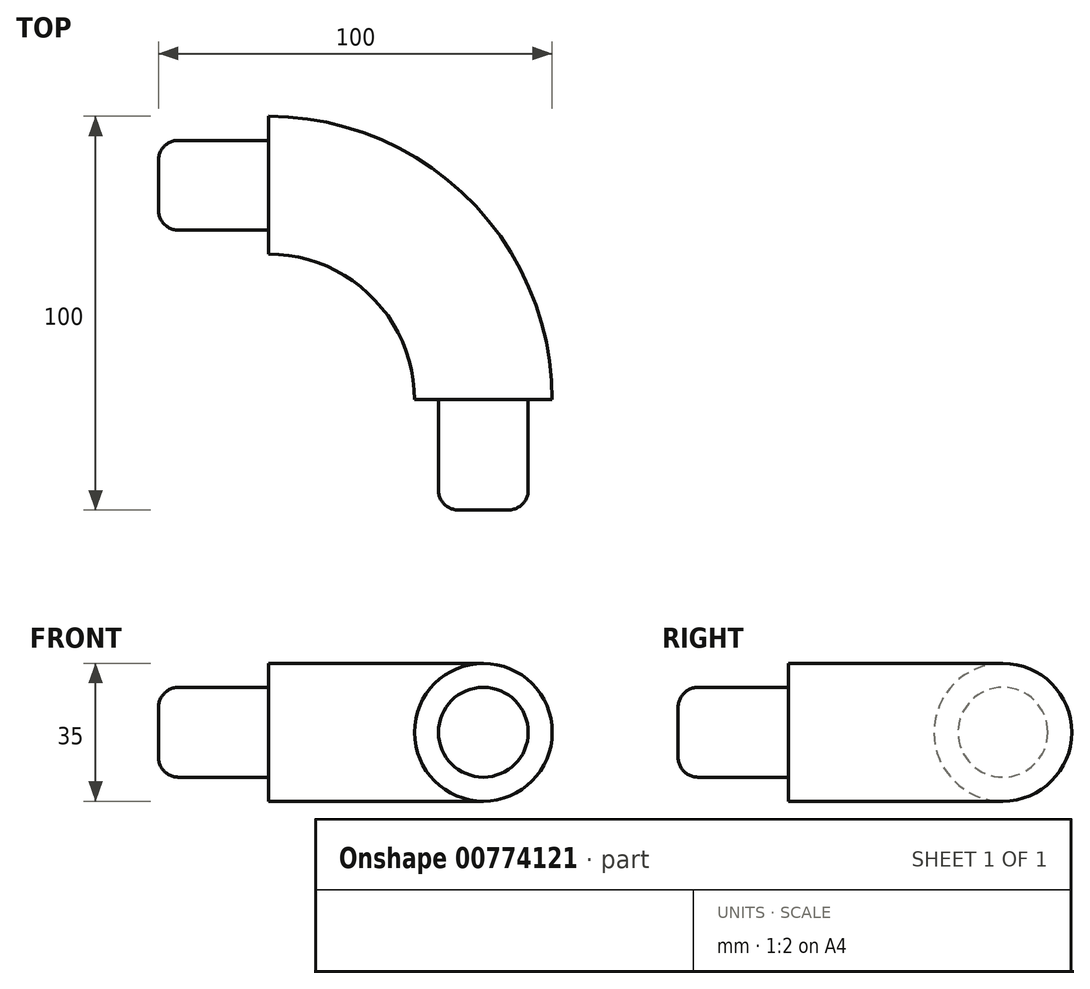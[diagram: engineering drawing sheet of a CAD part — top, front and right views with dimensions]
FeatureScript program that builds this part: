
annotation { "Feature Type Name" : "Feature", "Feature Type Description" : "" }
export const myFeature = defineFeature(function(context is Context, id is Id, definition is map)
    precondition{}
    {
        {
            var Q0;
            Q0=qCreatedBy(makeId("Top.planeOp"),FACE);
            var sketch = newSketch(context, id + "F0", { "sketchPlane" : qUnion([Q0])});
            skArc(sketch, "E0", {"start": v(0, 54.5) * mm, "mid": v(38.54, 38.54) * mm, "end": v(54.5, 0) * mm});
            skSolve(sketch);
        }
        {
            var Q0;
            Q0=qCreatedBy(makeId("Right.planeOp"),FACE);
            var sketch = newSketch(context, id + "F1", { "sketchPlane" : qUnion([Q0])});
            skCircle(sketch, "E1", {"center": v(54.5, 0) * mm, "radius": 17.5 * mm});
            skSolve(sketch);
        }
        {
            var Q0;
            Q0=makeQuery(id+"F1.imprint","IMPRINT",FACE,{"disambiguationData":[TD([[makeQuery(id+"F1.imprint","IMPRINT",EDGE,{"derivedFrom":sQuery(id+"F1.wireOp",EDGE,"E1")}),1.0]])]});
            var Q1;
            Q1=sQuery(id+"F0.wireOp",EDGE,"E0");
            sweep(context, id + "F2", {"profiles" : qUnion([Q0]), "path" : qUnion([Q1])});
        }
        {
            var Q0;
            Q0=makeQuery(id+"F2.opSweep","CAP_FACE",FACE,{"disambiguationData":[OSD([sQuery(id+"F0.wireOp",VERTEX,"E0.end"),sQuery(id+"F1.wireOp",EDGE,"E1")])],"isStart":false});
            var sketch = newSketch(context, id + "F3", { "sketchPlane" : qUnion([Q0])});
            skCircle(sketch, "E2", {"center": v(54.5, 0) * mm, "radius": 11.4 * mm});
            skSolve(sketch);
        }
        {
            var Q0;
            Q0 = qSketchRegion(id + "F3", true);
            extrude(context, id + "F4", {"entities" : qUnion([Q0]), "operationType" : NewBodyOperationType.ADD, "depth" : 28 * mm, "offsetDistance" : 25 * mm});
        }
        {
            var Q0;
            Q0=makeQuery(id+"F2.opSweep","CAP_FACE",FACE,{"disambiguationData":[OSD([sQuery(id+"F0.wireOp",VERTEX,"E0.start"),sQuery(id+"F1.wireOp",EDGE,"E1")])],"isStart":true});
            var sketch = newSketch(context, id + "F5", { "sketchPlane" : qUnion([Q0])});
            skCircle(sketch, "E3", {"center": v(-54.5, 0) * mm, "radius": 11.4 * mm});
            skSolve(sketch);
        }
        {
            var Q0;
            Q0 = qSketchRegion(id + "F5", true);
            extrude(context, id + "F6", {"entities" : qUnion([Q0]), "operationType" : NewBodyOperationType.ADD, "depth" : 28 * mm, "offsetDistance" : 25 * mm});
        }
        {
            var Q0;
            Q0=makeQuery(id+"F4.opExtrude","CAP_EDGE",EDGE,{"disambiguationData":[OSD([sQuery(id+"F3.wireOp",EDGE,"E2")])],"isStart":false});
            fillet(context, id + "F7", {"entities" : qUnion([Q0]), "radius" : 5 * mm, "tangentPropagation" : true, "allowEdgeOverflow" : false});
        }
        {
            var Q0;
            Q0=makeQuery(id+"F6.opExtrude","CAP_EDGE",EDGE,{"disambiguationData":[OSD([sQuery(id+"F5.wireOp",EDGE,"E3")])],"isStart":false});
            fillet(context, id + "F8", {"entities" : qUnion([Q0]), "radius" : 5 * mm, "tangentPropagation" : true, "allowEdgeOverflow" : false});
        }
    });
